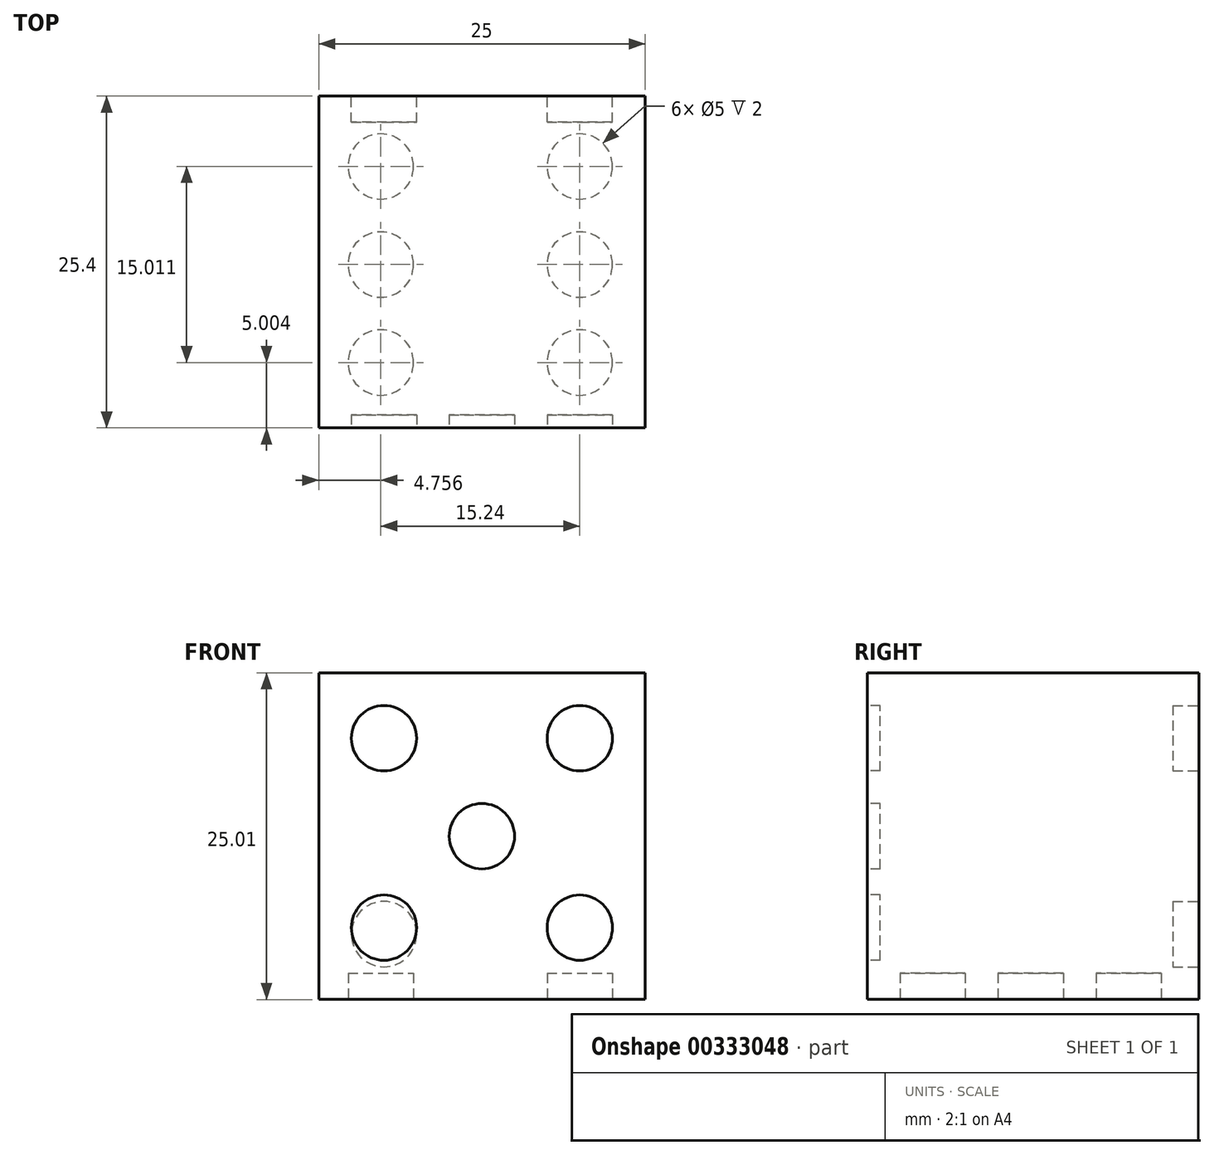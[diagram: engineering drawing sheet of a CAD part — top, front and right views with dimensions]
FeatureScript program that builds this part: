
annotation { "Feature Type Name" : "Feature", "Feature Type Description" : "" }
export const myFeature = defineFeature(function(context is Context, id is Id, definition is map)
    precondition{}
    {
        {
            var Q0;
            Q0=qCreatedBy(makeId("Front.planeOp"),FACE);
            var sketch = newSketch(context, id + "F0", { "sketchPlane" : qUnion([Q0])});
            skLineSegment(sketch, "E0.bottom", {"start": v(-25, 37.13) * mm, "end": v(0, 37.13) * mm});
            skLineSegment(sketch, "E0.top", {"start": v(-25, 12.13) * mm, "end": v(0, 12.13) * mm});
            skLineSegment(sketch, "E0.left", {"start": v(-25, 37.13) * mm, "end": v(-25, 12.13) * mm});
            skLineSegment(sketch, "E0.right", {"start": v(0, 37.13) * mm, "end": v(0, 12.13) * mm});
            skSolve(sketch);
        }
        {
            var Q0;
            Q0=makeQuery(id+"F0.imprint","IMPRINT",FACE,{"disambiguationData":[TD([[makeQuery(id+"F0.imprint","IMPRINT",EDGE,{"derivedFrom":sQuery(id+"F0.wireOp",EDGE,"E0.bottom")}),-1.0]])]});
            extrude(context, id + "F1", {"entities" : qUnion([Q0]), "depth" : 25.4 * mm});
        }
        {
            var Q0;
            Q0=makeQuery(id+"F1.opExtrude","CAP_FACE",FACE,{"disambiguationData":[OSD([sQuery(id+"F0.wireOp",EDGE,"E0.bottom"),sQuery(id+"F0.wireOp",EDGE,"E0.top"),sQuery(id+"F0.wireOp",EDGE,"E0.left"),sQuery(id+"F0.wireOp",EDGE,"E0.right")])],"isStart":false});
            var sketch = newSketch(context, id + "F2", { "sketchPlane" : qUnion([Q0])});
            skCircle(sketch, "E1", {"center": v(-20, 32.13) * mm, "radius": 2.5 * mm});
            skCircle(sketch, "E2", {"center": v(-20, 17.63) * mm, "radius": 2.5 * mm});
            skCircle(sketch, "E3", {"center": v(-5, 32.12) * mm, "radius": 2.5 * mm});
            skCircle(sketch, "E4", {"center": v(-5, 17.63) * mm, "radius": 2.5 * mm});
            skCircle(sketch, "E5", {"center": v(-12.5, 24.63) * mm, "radius": 2.5 * mm});
            skSolve(sketch);
        }
        {
            var Q0;
            Q0=makeQuery(id+"F2.imprint","IMPRINT",FACE,{"disambiguationData":[TD([[makeQuery(id+"F2.imprint","IMPRINT",EDGE,{"derivedFrom":sQuery(id+"F2.wireOp",EDGE,"E1")}),1.0]])]});
            var Q1;
            Q1=makeQuery(id+"F2.imprint","IMPRINT",FACE,{"disambiguationData":[TD([[makeQuery(id+"F2.imprint","IMPRINT",EDGE,{"derivedFrom":sQuery(id+"F2.wireOp",EDGE,"E5")}),1.0]])]});
            var Q2;
            Q2=makeQuery(id+"F2.imprint","IMPRINT",FACE,{"disambiguationData":[TD([[makeQuery(id+"F2.imprint","IMPRINT",EDGE,{"derivedFrom":sQuery(id+"F2.wireOp",EDGE,"E3")}),1.0]])]});
            var Q3;
            Q3=makeQuery(id+"F2.imprint","IMPRINT",FACE,{"disambiguationData":[TD([[makeQuery(id+"F2.imprint","IMPRINT",EDGE,{"derivedFrom":sQuery(id+"F2.wireOp",EDGE,"E4")}),1.0]])]});
            var Q4;
            Q4=makeQuery(id+"F2.imprint","IMPRINT",FACE,{"disambiguationData":[TD([[makeQuery(id+"F2.imprint","IMPRINT",EDGE,{"derivedFrom":sQuery(id+"F2.wireOp",EDGE,"E2")}),1.0]])]});
            extrude(context, id + "F3", {"entities" : qUnion([Q0, Q1, Q2, Q3, Q4]), "operationType" : NewBodyOperationType.REMOVE, "oppositeDirection" : true, "depth" : 1 * mm});
        }
        {
            var Q0;
            Q0=makeQuery(id+"F1.opExtrude","CAP_FACE",FACE,{"disambiguationData":[OSD([sQuery(id+"F0.wireOp",EDGE,"E0.bottom"),sQuery(id+"F0.wireOp",EDGE,"E0.top"),sQuery(id+"F0.wireOp",EDGE,"E0.left"),sQuery(id+"F0.wireOp",EDGE,"E0.right")])],"isStart":true});
            var sketch = newSketch(context, id + "F4", { "sketchPlane" : qUnion([Q0])});
            skCircle(sketch, "E6", {"center": v(5, 32.12) * mm, "radius": 2.5 * mm});
            skCircle(sketch, "E7", {"center": v(20, 17.13) * mm, "radius": 2.5 * mm});
            skSolve(sketch);
        }
        {
            var Q0;
            Q0=makeQuery(id+"F4.imprint","IMPRINT",FACE,{"disambiguationData":[TD([[makeQuery(id+"F4.imprint","IMPRINT",EDGE,{"derivedFrom":sQuery(id+"F4.wireOp",EDGE,"E6")}),1.0]])]});
            var Q1;
            Q1=makeQuery(id+"F4.imprint","IMPRINT",FACE,{"disambiguationData":[TD([[makeQuery(id+"F4.imprint","IMPRINT",EDGE,{"derivedFrom":sQuery(id+"F4.wireOp",EDGE,"E7")}),1.0]])]});
            extrude(context, id + "F5", {"entities" : qUnion([Q0, Q1]), "operationType" : NewBodyOperationType.REMOVE, "oppositeDirection" : true, "depth" : 2 * mm});
        }
        {
            var Q0;
            Q0=makeQuery(id+"F1.opExtrude","SWEPT_FACE",FACE,{"disambiguationData":[OSD([sQuery(id+"F0.wireOp",EDGE,"E0.top")])]});
            var sketch = newSketch(context, id + "F6", { "sketchPlane" : qUnion([Q0])});
            skCircle(sketch, "E8", {"center": v(-5, 5.38) * mm, "radius": 2.5 * mm});
            skCircle(sketch, "E9", {"center": v(-5, 12.9) * mm, "radius": 2.5 * mm});
            skCircle(sketch, "E10", {"center": v(-5, 20.4) * mm, "radius": 2.5 * mm});
            skCircle(sketch, "E11.1.0.0", {"center": v(-20.24, 5.38) * mm, "radius": 2.5 * mm});
            skCircle(sketch, "E11.1.0.1", {"center": v(-20.24, 12.9) * mm, "radius": 2.5 * mm});
            skCircle(sketch, "E11.1.0.2", {"center": v(-20.24, 20.4) * mm, "radius": 2.5 * mm});
            skLineSegment(sketch, "E11.direction1", {"start": v(-5, 5.38) * mm, "end": v(-20.24, 5.38) * mm, "construction": true});
            skSolve(sketch);
        }
        {
            var Q0;
            Q0=makeQuery(id+"F6.imprint","IMPRINT",FACE,{"disambiguationData":[TD([[makeQuery(id+"F6.imprint","IMPRINT",EDGE,{"derivedFrom":sQuery(id+"F6.wireOp",EDGE,"E8")}),1.0]])]});
            var Q1;
            Q1=makeQuery(id+"F6.imprint","IMPRINT",FACE,{"disambiguationData":[TD([[makeQuery(id+"F6.imprint","IMPRINT",EDGE,{"derivedFrom":sQuery(id+"F6.wireOp",EDGE,"E11.1.0.1")}),1.0]])]});
            var Q2;
            Q2=makeQuery(id+"F6.imprint","IMPRINT",FACE,{"disambiguationData":[TD([[makeQuery(id+"F6.imprint","IMPRINT",EDGE,{"derivedFrom":sQuery(id+"F6.wireOp",EDGE,"E9")}),1.0]])]});
            var Q3;
            Q3=makeQuery(id+"F6.imprint","IMPRINT",FACE,{"disambiguationData":[TD([[makeQuery(id+"F6.imprint","IMPRINT",EDGE,{"derivedFrom":sQuery(id+"F6.wireOp",EDGE,"E10")}),1.0]])]});
            var Q4;
            Q4=makeQuery(id+"F6.imprint","IMPRINT",FACE,{"disambiguationData":[TD([[makeQuery(id+"F6.imprint","IMPRINT",EDGE,{"derivedFrom":sQuery(id+"F6.wireOp",EDGE,"E11.1.0.2")}),1.0]])]});
            var Q5;
            Q5=makeQuery(id+"F6.imprint","IMPRINT",FACE,{"disambiguationData":[TD([[makeQuery(id+"F6.imprint","IMPRINT",EDGE,{"derivedFrom":sQuery(id+"F6.wireOp",EDGE,"E11.1.0.0")}),1.0]])]});
            extrude(context, id + "F7", {"entities" : qUnion([Q0, Q1, Q2, Q3, Q4, Q5]), "operationType" : NewBodyOperationType.REMOVE, "oppositeDirection" : true, "depth" : 2 * mm});
        }
    });
